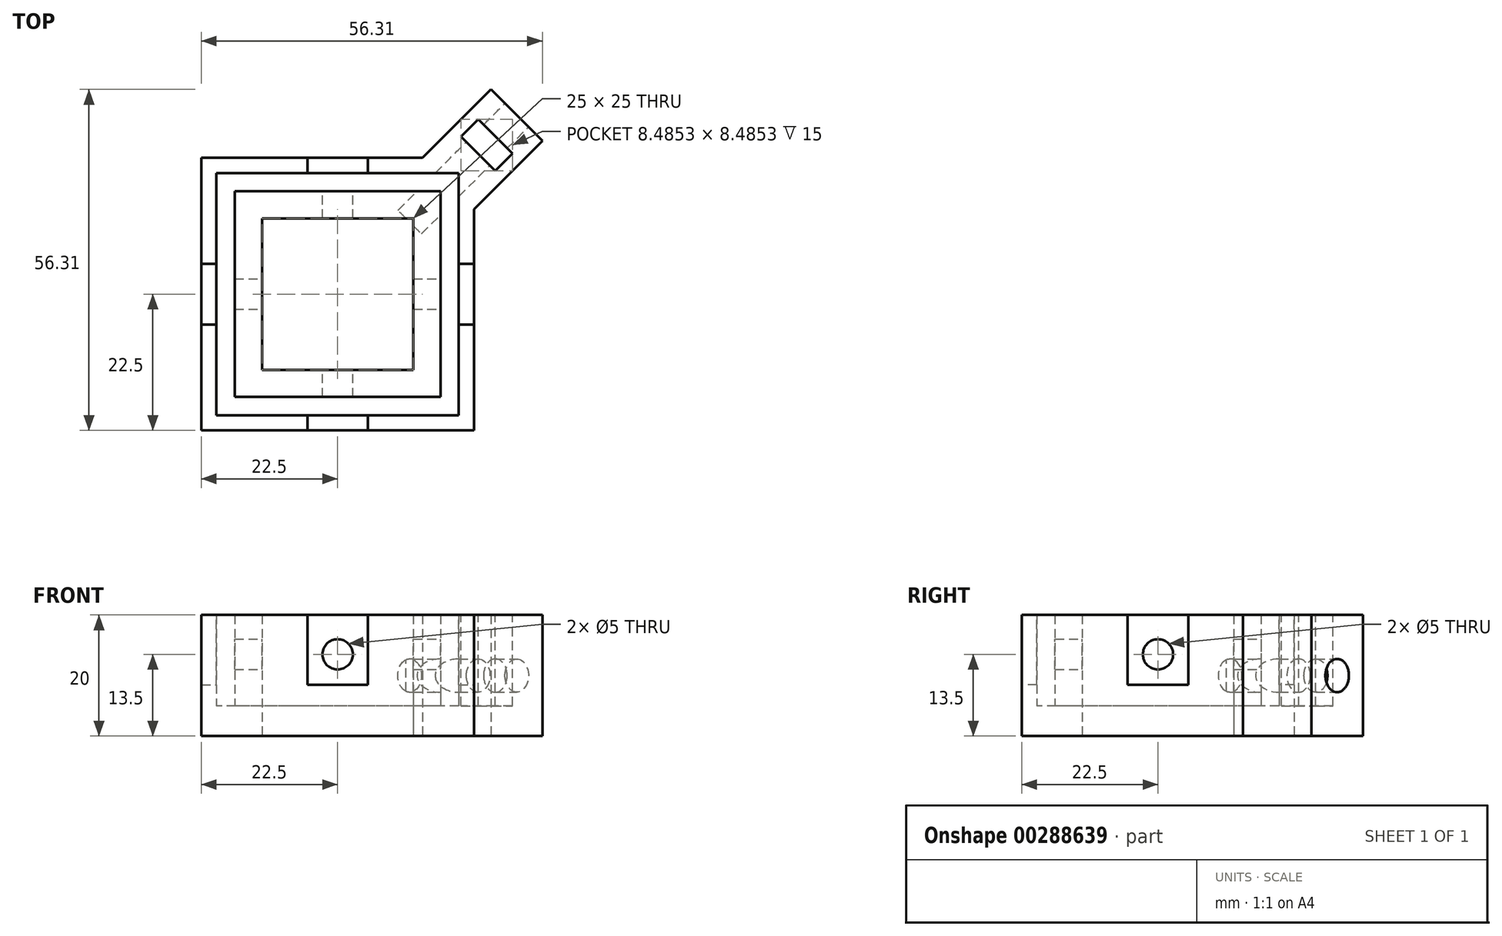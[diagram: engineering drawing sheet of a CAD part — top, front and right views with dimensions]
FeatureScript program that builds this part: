
annotation { "Feature Type Name" : "Feature", "Feature Type Description" : "" }
export const myFeature = defineFeature(function(context is Context, id is Id, definition is map)
    precondition{}
    {
        {
            var Q0;
            Q0=qCreatedBy(makeId("Top.planeOp"),FACE);
            var sketch = newSketch(context, id + "F0", { "sketchPlane" : qUnion([Q0])});
            skLineSegment(sketch, "E0.bottom", {"start": v(12.5, 12.5) * mm, "end": v(-12.5, 12.5) * mm});
            skLineSegment(sketch, "E0.top", {"start": v(12.5, -12.5) * mm, "end": v(-12.5, -12.5) * mm});
            skLineSegment(sketch, "E0.left", {"start": v(12.5, 12.5) * mm, "end": v(12.5, -12.5) * mm});
            skLineSegment(sketch, "E0.right", {"start": v(-12.5, 12.5) * mm, "end": v(-12.5, -12.5) * mm});
            skPoint(sketch, "E0.middle", {"position": v(0, 0) * mm});
            skLineSegment(sketch, "E1.bottom", {"start": v(22.5, 22.5) * mm, "end": v(-22.5, 22.5) * mm});
            skLineSegment(sketch, "E1.top", {"start": v(22.5, -22.5) * mm, "end": v(-22.5, -22.5) * mm});
            skLineSegment(sketch, "E1.left", {"start": v(22.5, 22.5) * mm, "end": v(22.5, -22.5) * mm});
            skLineSegment(sketch, "E1.right", {"start": v(-22.5, 22.5) * mm, "end": v(-22.5, -22.5) * mm});
            skLineSegment(sketch, "E2", {"start": v(14.01, 22.5) * mm, "end": v(25.33, 33.81) * mm});
            skLineSegment(sketch, "E3", {"start": v(25.33, 33.81) * mm, "end": v(33.81, 25.33) * mm});
            skLineSegment(sketch, "E4", {"start": v(33.81, 25.33) * mm, "end": v(22.5, 14.01) * mm});
            skSolve(sketch);
        }
        {
            var Q0;
            Q0=makeQuery(id+"F0.imprint","IMPRINT",FACE,{"disambiguationData":[TD([[makeQuery(id+"F0.imprint","IMPRINT",EDGE,{"derivedFrom":sQuery(id+"F0.wireOp",EDGE,"E0.bottom")}),-1.0]])]});
            var Q1;
            {var subQ0=sQuery(id+"F0.wireOp",EDGE,"E2");Q1=makeQuery(id+"F0.imprint","IMPRINT",FACE,{"disambiguationData":[TD([[makeQuery(id+"F0.imprint","IMPRINT",EDGE,{"derivedFrom":subQ0}),-1.0]])]});}
            extrude(context, id + "F1", {"entities" : qUnion([Q0, Q1]), "depth" : 5 * mm});
        }
        {
            var Q0;
            Q0=makeQuery(id+"F1.opExtrude","CAP_FACE",FACE,{"disambiguationData":[OSD([sQuery(id+"F0.wireOp",EDGE,"E0.bottom"),sQuery(id+"F0.wireOp",EDGE,"E0.top"),sQuery(id+"F0.wireOp",EDGE,"E0.left"),sQuery(id+"F0.wireOp",EDGE,"E0.right"),sQuery(id+"F0.wireOp",EDGE,"E1.bottom"),sQuery(id+"F0.wireOp",EDGE,"E1.top"),sQuery(id+"F0.wireOp",EDGE,"E1.left"),sQuery(id+"F0.wireOp",EDGE,"E1.right")])],"isStart":false});
            var sketch = newSketch(context, id + "F2", { "sketchPlane" : qUnion([Q0])});
            skLineSegment(sketch, "E5.bottom", {"start": v(17, 17) * mm, "end": v(-17, 17) * mm});
            skLineSegment(sketch, "E5.top", {"start": v(17, -17) * mm, "end": v(-17, -17) * mm});
            skLineSegment(sketch, "E5.left", {"start": v(17, 17) * mm, "end": v(17, -17) * mm});
            skLineSegment(sketch, "E5.right", {"start": v(-17, 17) * mm, "end": v(-17, -17) * mm});
            skPoint(sketch, "E5.middle", {"position": v(0, 0) * mm});
            skSolve(sketch);
        }
        {
            var Q0;
            Q0=makeQuery(id+"F2.imprint","IMPRINT",FACE,{"disambiguationData":[TD([[makeQuery(id+"F2.imprint","IMPRINT",EDGE,{"derivedFrom":sQuery(id+"F2.wireOp",EDGE,"E5.bottom")}),1.0]])]});
            extrude(context, id + "F3", {"entities" : qUnion([Q0]), "operationType" : NewBodyOperationType.ADD, "depth" : 15 * mm});
        }
        {
            var Q0;
            Q0=makeQuery(id+"F1.opExtrude","CAP_FACE",FACE,{"disambiguationData":[OSD([sQuery(id+"F0.wireOp",EDGE,"E0.bottom"),sQuery(id+"F0.wireOp",EDGE,"E0.top"),sQuery(id+"F0.wireOp",EDGE,"E0.left"),sQuery(id+"F0.wireOp",EDGE,"E0.right"),sQuery(id+"F0.wireOp",EDGE,"E1.bottom"),sQuery(id+"F0.wireOp",EDGE,"E1.top"),sQuery(id+"F0.wireOp",EDGE,"E1.left"),sQuery(id+"F0.wireOp",EDGE,"E1.right")])],"isStart":false});
            var sketch = newSketch(context, id + "F4", { "sketchPlane" : qUnion([Q0])});
            skLineSegment(sketch, "E6.bottom", {"start": v(20, 20) * mm, "end": v(-20, 20) * mm});
            skLineSegment(sketch, "E6.top", {"start": v(20, -20) * mm, "end": v(-20, -20) * mm});
            skLineSegment(sketch, "E6.left", {"start": v(20, 20) * mm, "end": v(20, -20) * mm});
            skLineSegment(sketch, "E6.right", {"start": v(-20, 20) * mm, "end": v(-20, -20) * mm});
            skPoint(sketch, "E6.middle", {"position": v(0, 0) * mm});
            skSolve(sketch);
        }
        {
            var Q0;
            Q0=makeQuery(id+"F4.imprint","IMPRINT",FACE,{"disambiguationData":[TD([[makeQuery(id+"F4.imprint","IMPRINT",EDGE,{"derivedFrom":sQuery(id+"F4.wireOp",EDGE,"E6.bottom")}),-1.0]])]});
            extrude(context, id + "F5", {"entities" : qUnion([Q0]), "operationType" : NewBodyOperationType.ADD, "depth" : 15 * mm});
        }
        {
            var Q0;
            Q0=makeQuery(id+"F5.opExtrude","CAP_FACE",FACE,{"disambiguationData":[OSD([sQuery(id+"F0.wireOp",EDGE,"E1.bottom"),sQuery(id+"F0.wireOp",EDGE,"E1.top"),sQuery(id+"F0.wireOp",EDGE,"E1.left"),sQuery(id+"F0.wireOp",EDGE,"E1.right"),sQuery(id+"F4.wireOp",EDGE,"E6.bottom"),sQuery(id+"F4.wireOp",EDGE,"E6.top"),sQuery(id+"F4.wireOp",EDGE,"E6.left"),sQuery(id+"F4.wireOp",EDGE,"E6.right")])],"isStart":false});
            var sketch = newSketch(context, id + "F6", { "sketchPlane" : qUnion([Q0])});
            skLineSegment(sketch, "E7.bottom", {"start": v(-5, 22.5) * mm, "end": v(5, 22.5) * mm});
            skLineSegment(sketch, "E7.top", {"start": v(-5, 20) * mm, "end": v(5, 20) * mm});
            skLineSegment(sketch, "E7.left", {"start": v(-5, 22.5) * mm, "end": v(-5, 20) * mm});
            skLineSegment(sketch, "E7.right", {"start": v(5, 22.5) * mm, "end": v(5, 20) * mm});
            skLineSegment(sketch, "E8.bottom", {"start": v(-22.5, 5) * mm, "end": v(-20, 5) * mm});
            skLineSegment(sketch, "E8.top", {"start": v(-22.5, -5) * mm, "end": v(-20, -5) * mm});
            skLineSegment(sketch, "E8.left", {"start": v(-22.5, 5) * mm, "end": v(-22.5, -5) * mm});
            skLineSegment(sketch, "E8.right", {"start": v(-20, 5) * mm, "end": v(-20, -5) * mm});
            skLineSegment(sketch, "E9.bottom", {"start": v(20, 5) * mm, "end": v(22.5, 5) * mm});
            skLineSegment(sketch, "E9.top", {"start": v(20, -5) * mm, "end": v(22.5, -5) * mm});
            skLineSegment(sketch, "E9.left", {"start": v(20, 5) * mm, "end": v(20, -5) * mm});
            skLineSegment(sketch, "E9.right", {"start": v(22.5, 5) * mm, "end": v(22.5, -5) * mm});
            skLineSegment(sketch, "E10.bottom", {"start": v(-5, -20) * mm, "end": v(5, -20) * mm});
            skLineSegment(sketch, "E10.top", {"start": v(-5, -22.5) * mm, "end": v(5, -22.5) * mm});
            skLineSegment(sketch, "E10.left", {"start": v(-5, -20) * mm, "end": v(-5, -22.5) * mm});
            skLineSegment(sketch, "E10.right", {"start": v(5, -20) * mm, "end": v(5, -22.5) * mm});
            skSolve(sketch);
        }
        {
            var Q0;
            Q0 = qSketchRegion(id + "F6", true);
            extrude(context, id + "F7", {"entities" : qUnion([Q0]), "operationType" : NewBodyOperationType.REMOVE, "oppositeDirection" : true, "depth" : 11.5 * mm, "offsetDistance" : 25 * mm});
        }
        {
            var Q0;
            {var subQ0=sQuery(id+"F0.wireOp",EDGE,"E3");Q0=makeQuery(id+"F5.boolean.opBoolean","MERGE",FACE,{"derivedFrom":[makeQuery(id+"F1.opExtrude","SWEPT_FACE",FACE,{"disambiguationData":[OSD([subQ0])]}),makeQuery(id+"F5.opExtrude","SWEPT_FACE",FACE,{"disambiguationData":[OSD([subQ0])]})]});}
            var sketch = newSketch(context, id + "F8", { "sketchPlane" : qUnion([Q0])});
            skCircle(sketch, "E11", {"center": v(0, 10) * mm, "radius": 2.75 * mm});
            skSolve(sketch);
        }
        {
            var Q0;
            Q0=makeQuery(id+"F8.imprint","IMPRINT",FACE,{"disambiguationData":[TD([[makeQuery(id+"F8.imprint","IMPRINT",EDGE,{"derivedFrom":sQuery(id+"F8.wireOp",EDGE,"E11")}),1.0]])]});
            extrude(context, id + "F9", {"entities" : qUnion([Q0]), "operationType" : NewBodyOperationType.REMOVE, "oppositeDirection" : true, "depth" : 25 * mm});
        }
        {
            var Q0;
            {var subQ0=sQuery(id+"F0.wireOp",EDGE,"E2");var subQ1=sQuery(id+"F0.wireOp",EDGE,"E1.left");var subQ2=sQuery(id+"F0.wireOp",EDGE,"E1.bottom");var subQ3=sQuery(id+"F0.wireOp",EDGE,"E4");var subQ4=sQuery(id+"F4.wireOp",EDGE,"E6.bottom");var subQ5=sQuery(id+"F0.wireOp",EDGE,"E3");var subQ6=sQuery(id+"F4.wireOp",EDGE,"E6.left");Q0=makeQuery(id+"F7.boolean.opBoolean","SPLIT",FACE,{"disambiguationData":[TD([makeQuery(id+"F1.opExtrude","SWEPT_FACE",FACE,{"disambiguationData":[OSD([subQ0])]})])],"derivedFrom":makeQuery(id+"F5.opExtrude","CAP_FACE",FACE,{"disambiguationData":[OSD([subQ2,sQuery(id+"F0.wireOp",EDGE,"E1.top"),subQ1,sQuery(id+"F0.wireOp",EDGE,"E1.right"),subQ0,subQ5,subQ3,subQ4,sQuery(id+"F4.wireOp",EDGE,"E6.top"),subQ6,sQuery(id+"F4.wireOp",EDGE,"E6.right")])],"isStart":false})});}
            var sketch = newSketch(context, id + "F10", { "sketchPlane" : qUnion([Q0])});
            skLineSegment(sketch, "E12", {"start": v(23.2, 28.86) * mm, "end": v(28.86, 23.2) * mm});
            skLineSegment(sketch, "E13", {"start": v(28.86, 23.2) * mm, "end": v(26.04, 20.38) * mm});
            skLineSegment(sketch, "E14", {"start": v(26.04, 20.38) * mm, "end": v(20.38, 26.04) * mm});
            skLineSegment(sketch, "E15", {"start": v(20.38, 26.04) * mm, "end": v(23.2, 28.86) * mm});
            skSolve(sketch);
        }
        {
            var Q0;
            Q0=makeQuery(id+"F10.imprint","IMPRINT",FACE,{"disambiguationData":[TD([[makeQuery(id+"F10.imprint","IMPRINT",EDGE,{"derivedFrom":sQuery(id+"F10.wireOp",EDGE,"E12")}),-1.0]])]});
            extrude(context, id + "F11", {"entities" : qUnion([Q0]), "operationType" : NewBodyOperationType.REMOVE, "oppositeDirection" : true, "depth" : 15 * mm});
        }
        {
            var Q0;
            Q0=makeQuery(id+"F3.opExtrude","SWEPT_FACE",FACE,{"disambiguationData":[OSD([sQuery(id+"F2.wireOp",EDGE,"E5.bottom")])]});
            var sketch = newSketch(context, id + "F12", { "sketchPlane" : qUnion([Q0])});
            skCircle(sketch, "E16", {"center": v(0, 13.5) * mm, "radius": 2.5 * mm});
            skPoint(sketch, "E16.centerSnap0", {"position": v(0, 20) * mm});
            skSolve(sketch);
        }
        {
            var Q0;
            Q0=makeQuery(id+"F12.imprint","IMPRINT",FACE,{"disambiguationData":[TD([[makeQuery(id+"F12.imprint","IMPRINT",EDGE,{"derivedFrom":sQuery(id+"F12.wireOp",EDGE,"E16")}),1.0]])]});
            extrude(context, id + "F13", {"entities" : qUnion([Q0]), "operationType" : NewBodyOperationType.REMOVE, "oppositeDirection" : true, "depth" : 45 * mm, "offsetDistance" : 25 * mm});
        }
        {
            var Q0;
            Q0=makeQuery(id+"F3.opExtrude","SWEPT_FACE",FACE,{"disambiguationData":[OSD([sQuery(id+"F2.wireOp",EDGE,"E5.left")])]});
            var sketch = newSketch(context, id + "F14", { "sketchPlane" : qUnion([Q0])});
            skCircle(sketch, "E17", {"center": v(0, 13.5) * mm, "radius": 2.5 * mm});
            skPoint(sketch, "E17.centerSnap0", {"position": v(0, 20) * mm});
            skSolve(sketch);
        }
        {
            var Q0;
            Q0=makeQuery(id+"F14.imprint","IMPRINT",FACE,{"disambiguationData":[TD([[makeQuery(id+"F14.imprint","IMPRINT",EDGE,{"derivedFrom":sQuery(id+"F14.wireOp",EDGE,"E17")}),1.0]])]});
            extrude(context, id + "F15", {"entities" : qUnion([Q0]), "operationType" : NewBodyOperationType.REMOVE, "oppositeDirection" : true, "depth" : 45 * mm, "offsetDistance" : 25 * mm});
        }
    });
